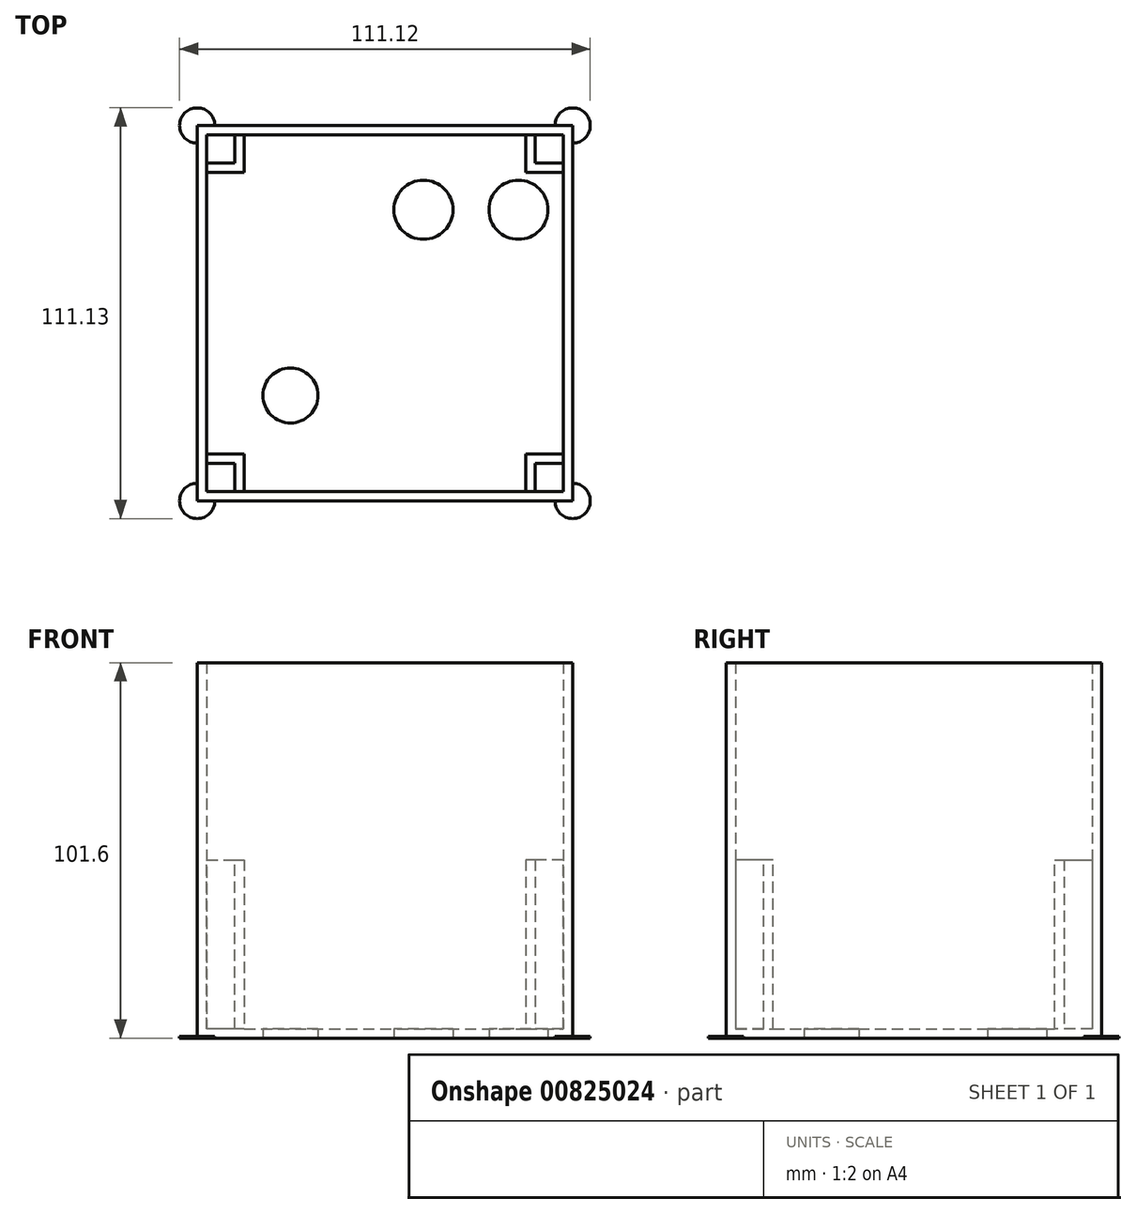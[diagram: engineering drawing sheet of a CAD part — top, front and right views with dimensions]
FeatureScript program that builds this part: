
annotation { "Feature Type Name" : "Feature", "Feature Type Description" : "" }
export const myFeature = defineFeature(function(context is Context, id is Id, definition is map)
    precondition{}
    {
        {
            var Q0;
            Q0=qCreatedBy(makeId("Top.planeOp"),FACE);
            var sketch = newSketch(context, id + "F0", { "sketchPlane" : qUnion([Q0])});
            skLineSegment(sketch, "E0", {"start": v(-58.83, 18.55) * mm, "end": v(-58.83, -83.05) * mm});
            skLineSegment(sketch, "E1", {"start": v(-58.83, -83.05) * mm, "end": v(42.77, -83.05) * mm});
            skLineSegment(sketch, "E2", {"start": v(42.77, -83.05) * mm, "end": v(42.77, 18.55) * mm});
            skLineSegment(sketch, "E3", {"start": v(42.77, 18.55) * mm, "end": v(-58.83, 18.55) * mm});
            skCircle(sketch, "E4", {"center": v(2.38, -4.25) * mm, "radius": 8 * mm});
            skCircle(sketch, "E5", {"center": v(28.1, -4.25) * mm, "radius": 8 * mm});
            skLineSegment(sketch, "E6", {"start": v(-58.83, 5.85) * mm, "end": v(-46.13, 5.85) * mm});
            skLineSegment(sketch, "E7", {"start": v(-46.13, 5.85) * mm, "end": v(-46.13, 18.55) * mm});
            skLineSegment(sketch, "E8.MirrorCS", {"start": v(30.07, 5.85) * mm, "end": v(30.07, 18.55) * mm});
            skLineSegment(sketch, "E9.MirrorCS", {"start": v(42.77, 5.85) * mm, "end": v(30.07, 5.85) * mm});
            skLineSegment(sketch, "E10", {"start": v(-58.83, -32.25) * mm, "end": v(42.77, -32.25) * mm, "construction": true});
            skLineSegment(sketch, "E11.MirrorCS", {"start": v(-58.83, -70.35) * mm, "end": v(-46.13, -70.35) * mm});
            skLineSegment(sketch, "E12.MirrorCS", {"start": v(-46.13, -70.35) * mm, "end": v(-46.13, -83.05) * mm});
            skLineSegment(sketch, "E13.MirrorCS", {"start": v(42.77, -70.35) * mm, "end": v(30.07, -70.35) * mm});
            skLineSegment(sketch, "E14.MirrorCS", {"start": v(30.07, -70.35) * mm, "end": v(30.07, -83.05) * mm});
            skCircle(sketch, "E15", {"center": v(-33.6, -54.5) * mm, "radius": 7.45 * mm});
            skLineSegment(sketch, "E16", {"start": v(-8.03, -83.05) * mm, "end": v(-8.03, -32.25) * mm, "construction": true});
            skPoint(sketch, "E17", {"position": v(0, -54.5) * mm});
            skSolve(sketch);
        }
        {
            var Q0;
            Q0=makeQuery(id+"F0.imprint","IMPRINT",FACE,{"disambiguationData":[TD([[makeQuery(id+"F0.imprint","IMPRINT",EDGE,{"derivedFrom":sQuery(id+"F0.wireOp",EDGE,"E4")}),-1.0]])]});
            var Q1;
            {var subQ3=sQuery(id+"F0.wireOp",EDGE,"E11.MirrorCS");Q1=makeQuery(id+"F0.imprint","IMPRINT",FACE,{"disambiguationData":[TD([[makeQuery(id+"F0.imprint","IMPRINT",EDGE,{"derivedFrom":subQ3}),-1.0]])]});}
            var Q2;
            {var subQ3=sQuery(id+"F0.wireOp",EDGE,"E6");Q2=makeQuery(id+"F0.imprint","IMPRINT",FACE,{"disambiguationData":[TD([[makeQuery(id+"F0.imprint","IMPRINT",EDGE,{"derivedFrom":subQ3}),1.0]])]});}
            var Q3;
            {var subQ4=sQuery(id+"F0.wireOp",EDGE,"E13.MirrorCS");Q3=makeQuery(id+"F0.imprint","IMPRINT",FACE,{"disambiguationData":[TD([[makeQuery(id+"F0.imprint","IMPRINT",EDGE,{"derivedFrom":subQ4}),1.0]])]});}
            var Q4;
            {var subQ4=sQuery(id+"F0.wireOp",EDGE,"E8.MirrorCS");Q4=makeQuery(id+"F0.imprint","IMPRINT",FACE,{"disambiguationData":[TD([[makeQuery(id+"F0.imprint","IMPRINT",EDGE,{"derivedFrom":subQ4}),-1.0]])]});}
            extrude(context, id + "F1", {"entities" : qUnion([Q0, Q1, Q2, Q3, Q4]), "depth" : 101.6 * mm, "offsetDistance" : 25.4 * mm});
        }
        {
            var Q0;
            Q0=makeQuery(id+"F1.opExtrude","SWEPT_FACE",FACE,{"disambiguationData":[OSD([sQuery(id+"F0.wireOp",EDGE,"E4")])]});
            var Q1;
            Q1=makeQuery(id+"F1.opExtrude","SWEPT_FACE",FACE,{"disambiguationData":[OSD([sQuery(id+"F0.wireOp",EDGE,"E5")])]});
            var Q2;
            Q2=makeQuery(id+"F1.opExtrude","SWEPT_FACE",FACE,{"disambiguationData":[OSD([sQuery(id+"F0.wireOp",EDGE,"2a2af347-3364-40fd-80ae-ea958fc6cbd1")])]});
            var Q3;
            Q3=makeQuery(id+"F1.opExtrude","SWEPT_FACE",FACE,{"disambiguationData":[OSD([sQuery(id+"F0.wireOp",EDGE,"20077e1e-a13c-42d8-b34a-b8717fbbdf96")])]});
            var Q4;
            Q4=makeQuery(id+"F1.opExtrude","SWEPT_FACE",FACE,{"disambiguationData":[OSD([sQuery(id+"F0.wireOp",EDGE,"b74ed18e-008f-4efa-a3a0-238cff66c39b")])]});
            var Q5;
            Q5=makeQuery(id+"F1.opExtrude","SWEPT_FACE",FACE,{"disambiguationData":[OSD([sQuery(id+"F0.wireOp",EDGE,"305280a5-76a0-4ac1-98c7-6e3620a3919b")])]});
            var Q6;
            Q6=makeQuery(id+"F1.opExtrude","SWEPT_FACE",FACE,{"disambiguationData":[OSD([sQuery(id+"F0.wireOp",EDGE,"059d8431-9725-4e2a-9e9e-78c224f97e8a")])]});
            var Q7;
            Q7=makeQuery(id+"F1.opExtrude","CAP_FACE",FACE,{"disambiguationData":[OSD([sQuery(id+"F0.wireOp",EDGE,"E0"),sQuery(id+"F0.wireOp",EDGE,"E1"),sQuery(id+"F0.wireOp",EDGE,"E2"),sQuery(id+"F0.wireOp",EDGE,"E3"),sQuery(id+"F0.wireOp",EDGE,"E4"),sQuery(id+"F0.wireOp",EDGE,"E5"),sQuery(id+"F0.wireOp",EDGE,"E15")])],"isStart":false});
            var Q8;
            Q8=makeQuery(id+"F1.opExtrude","SWEPT_FACE",FACE,{"disambiguationData":[OSD([sQuery(id+"F0.wireOp",EDGE,"E15")])]});
            shell(context, id + "F2", {"entities" : qUnion([Q0, Q1, Q2, Q3, Q4, Q5, Q6, Q7, Q8]), "thickness" : 2.54 * mm});
        }
        {
            var Q0;
            Q0=makeQuery(id+"F0.imprint","IMPRINT",FACE,{"disambiguationData":[TD([[makeQuery(id+"F0.imprint","IMPRINT",EDGE,{"derivedFrom":sQuery(id+"F0.wireOp",EDGE,"E4")}),-1.0]])]});
            var sketch = newSketch(context, id + "F3", { "sketchPlane" : qUnion([Q0])});
            skLineSegment(sketch, "E18.0", {"start": v(-58.83, 5.85) * mm, "end": v(-46.13, 5.85) * mm});
            skLineSegment(sketch, "E19.0", {"start": v(-46.13, 5.85) * mm, "end": v(-46.13, 18.55) * mm});
            skLineSegment(sketch, "E20.0", {"start": v(30.07, 5.85) * mm, "end": v(30.07, 18.55) * mm});
            skLineSegment(sketch, "E21.0", {"start": v(42.77, 5.85) * mm, "end": v(30.07, 5.85) * mm});
            skLineSegment(sketch, "E22.0", {"start": v(42.77, -70.35) * mm, "end": v(30.07, -70.35) * mm});
            skLineSegment(sketch, "E23.0", {"start": v(30.07, -70.35) * mm, "end": v(30.07, -83.05) * mm});
            skLineSegment(sketch, "E24.0", {"start": v(-58.83, -70.35) * mm, "end": v(-46.13, -70.35) * mm});
            skLineSegment(sketch, "E25.0", {"start": v(-46.13, -70.35) * mm, "end": v(-46.13, -83.05) * mm});
            skLineSegment(sketch, "E26.0", {"start": v(-58.83, 18.55) * mm, "end": v(-58.83, -83.05) * mm});
            skLineSegment(sketch, "E27.0", {"start": v(-58.83, -83.05) * mm, "end": v(42.77, -83.05) * mm});
            skLineSegment(sketch, "E28.0", {"start": v(42.77, -83.05) * mm, "end": v(42.77, 18.55) * mm});
            skLineSegment(sketch, "E29.0", {"start": v(42.77, 18.55) * mm, "end": v(-58.83, 18.55) * mm});
            skSolve(sketch);
        }
        {
            var Q0;
            {var subQ0=sQuery(id+"F3.wireOp",EDGE,"E20.0");Q0=makeQuery(id+"F3.imprint","IMPRINT",FACE,{"disambiguationData":[TD([[makeQuery(id+"F3.imprint","IMPRINT",EDGE,{"derivedFrom":subQ0}),-1.0]])]});}
            var Q1;
            {var subQ4=sQuery(id+"F0.wireOp",EDGE,"E13.MirrorCS");Q1=makeQuery(id+"F0.imprint","IMPRINT",FACE,{"disambiguationData":[TD([[makeQuery(id+"F0.imprint","IMPRINT",EDGE,{"derivedFrom":subQ4}),1.0]])]});}
            var Q2;
            {var subQ0=sQuery(id+"F3.wireOp",EDGE,"E24.0");Q2=makeQuery(id+"F3.imprint","IMPRINT",FACE,{"disambiguationData":[TD([[makeQuery(id+"F3.imprint","IMPRINT",EDGE,{"derivedFrom":subQ0}),-1.0]])]});}
            var Q3;
            {var subQ0=sQuery(id+"F3.wireOp",EDGE,"E18.0");Q3=makeQuery(id+"F3.imprint","IMPRINT",FACE,{"disambiguationData":[TD([[makeQuery(id+"F3.imprint","IMPRINT",EDGE,{"derivedFrom":subQ0}),1.0]])]});}
            extrude(context, id + "F4", {"entities" : qUnion([Q0, Q1, Q2, Q3]), "operationType" : NewBodyOperationType.ADD, "depth" : 48.26 * mm, "offsetDistance" : 25.4 * mm});
        }
        {
            var Q0;
            Q0=makeQuery(id+"F4.opExtrude","CAP_FACE",FACE,{"disambiguationData":[OSD([sQuery(id+"F0.wireOp",EDGE,"E1"),sQuery(id+"F0.wireOp",EDGE,"E2"),sQuery(id+"F0.wireOp",EDGE,"E13.MirrorCS"),sQuery(id+"F0.wireOp",EDGE,"E14.MirrorCS")])],"isStart":false});
            var Q1;
            Q1=makeQuery(id+"F4.opExtrude","CAP_FACE",FACE,{"disambiguationData":[OSD([sQuery(id+"F3.wireOp",EDGE,"E24.0"),sQuery(id+"F3.wireOp",EDGE,"E25.0"),sQuery(id+"F3.wireOp",EDGE,"E26.0"),sQuery(id+"F3.wireOp",EDGE,"E27.0")])],"isStart":false});
            var Q2;
            Q2=makeQuery(id+"F4.opExtrude","CAP_FACE",FACE,{"disambiguationData":[OSD([sQuery(id+"F3.wireOp",EDGE,"E20.0"),sQuery(id+"F3.wireOp",EDGE,"E21.0"),sQuery(id+"F3.wireOp",EDGE,"E28.0"),sQuery(id+"F3.wireOp",EDGE,"E29.0")])],"isStart":false});
            var Q3;
            Q3=makeQuery(id+"F4.opExtrude","CAP_FACE",FACE,{"disambiguationData":[OSD([sQuery(id+"F3.wireOp",EDGE,"E18.0"),sQuery(id+"F3.wireOp",EDGE,"E19.0"),sQuery(id+"F3.wireOp",EDGE,"E26.0"),sQuery(id+"F3.wireOp",EDGE,"E29.0")])],"isStart":false});
            shell(context, id + "F5", {"entities" : qUnion([Q0, Q1, Q2, Q3]), "thickness" : 2.54 * mm});
        }
        {
            var Q0;
            Q0=makeQuery(id+"F0.imprint","IMPRINT",FACE,{"disambiguationData":[TD([[makeQuery(id+"F0.imprint","IMPRINT",EDGE,{"derivedFrom":sQuery(id+"F0.wireOp",EDGE,"E4")}),-1.0]])]});
            var sketch = newSketch(context, id + "F6", { "sketchPlane" : qUnion([Q0])});
            skCircle(sketch, "E30", {"center": v(-58.83, 18.55) * mm, "radius": 4.76 * mm});
            skCircle(sketch, "E31.0.1.0", {"center": v(-58.83, -83.05) * mm, "radius": 4.76 * mm});
            skCircle(sketch, "E31.1.0.0", {"center": v(42.77, 18.55) * mm, "radius": 4.76 * mm});
            skCircle(sketch, "E31.1.1.0", {"center": v(42.77, -83.05) * mm, "radius": 4.76 * mm});
            skLineSegment(sketch, "E31.direction1", {"start": v(-58.83, 18.55) * mm, "end": v(42.77, 18.55) * mm, "construction": true});
            skLineSegment(sketch, "E31.direction2", {"start": v(-58.83, 18.55) * mm, "end": v(-58.83, -83.05) * mm, "construction": true});
            skSolve(sketch);
        }
        {
            var Q0;
            Q0=makeQuery(id+"F6.imprint","IMPRINT",FACE,{"disambiguationData":[TD([[makeQuery(id+"F6.imprint","IMPRINT",EDGE,{"derivedFrom":sQuery(id+"F6.wireOp",EDGE,"E31.1.1.0")}),1.0]])]});
            var Q1;
            Q1=makeQuery(id+"F6.imprint","IMPRINT",FACE,{"disambiguationData":[TD([[makeQuery(id+"F6.imprint","IMPRINT",EDGE,{"derivedFrom":sQuery(id+"F6.wireOp",EDGE,"E31.0.1.0")}),1.0]])]});
            var Q2;
            Q2=makeQuery(id+"F6.imprint","IMPRINT",FACE,{"disambiguationData":[TD([[makeQuery(id+"F6.imprint","IMPRINT",EDGE,{"derivedFrom":sQuery(id+"F6.wireOp",EDGE,"E31.1.0.0")}),1.0]])]});
            var Q3;
            Q3=makeQuery(id+"F6.imprint","IMPRINT",FACE,{"disambiguationData":[TD([[makeQuery(id+"F6.imprint","IMPRINT",EDGE,{"derivedFrom":sQuery(id+"F6.wireOp",EDGE,"E30")}),1.0]])]});
            extrude(context, id + "F7", {"entities" : qUnion([Q0, Q1, Q2, Q3]), "operationType" : NewBodyOperationType.ADD, "depth" : .5 * mm, "offsetDistance" : 25.4 * mm});
        }
    });
